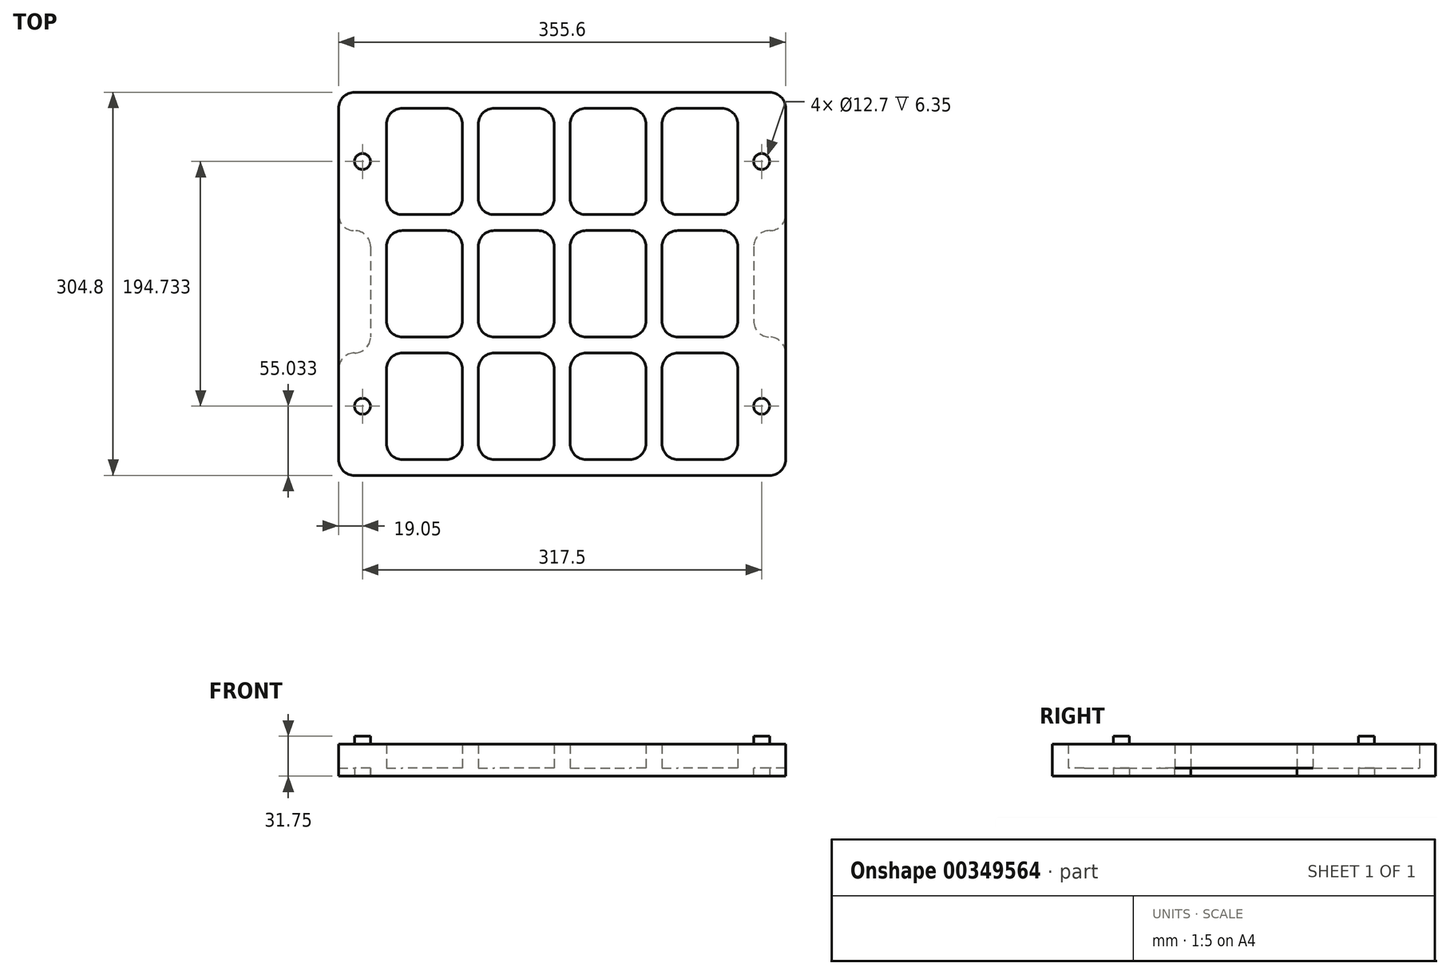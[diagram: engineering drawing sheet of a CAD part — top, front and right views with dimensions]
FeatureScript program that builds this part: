
annotation { "Feature Type Name" : "Feature", "Feature Type Description" : "" }
export const myFeature = defineFeature(function(context is Context, id is Id, definition is map)
    precondition{}
    {
        {
            var Q0;
            Q0=qCreatedBy(makeId("Top.planeOp"),FACE);
            var sketch = newSketch(context, id + "F0", { "sketchPlane" : qUnion([Q0])});
            skLineSegment(sketch, "E0.bottom", {"start": v(165.1, -152.4) * mm, "end": v(-165.1, -152.4) * mm});
            skLineSegment(sketch, "E0.top", {"start": v(165.1, 152.4) * mm, "end": v(-165.1, 152.4) * mm});
            skLineSegment(sketch, "E0.left", {"start": v(177.8, -139.7) * mm, "end": v(177.8, -55.03) * mm});
            skLineSegment(sketch, "E0.right", {"start": v(-177.8, -139.7) * mm, "end": v(-177.8, -67.73) * mm});
            skPoint(sketch, "E0.middle", {"position": v(0, 0) * mm});
            skLineSegment(sketch, "E1", {"start": v(-177.8, 55.03) * mm, "end": v(-177.8, 139.7) * mm});
            skLineSegment(sketch, "E2", {"start": v(177.8, 55.03) * mm, "end": v(177.8, 139.7) * mm});
            skPoint(sketch, "E3.visualSharp", {"position": v(-177.8, 152.4) * mm});
            skArc(sketch, "E3.filletArc", {"start": v(-165.1, 152.4) * mm, "mid": v(-174.08, 148.68) * mm, "end": v(-177.8, 139.7) * mm});
            skPoint(sketch, "E4.visualSharp", {"position": v(-177.8, -152.4) * mm});
            skArc(sketch, "E4.filletArc", {"start": v(-177.8, -139.7) * mm, "mid": v(-174.08, -148.68) * mm, "end": v(-165.1, -152.4) * mm});
            skPoint(sketch, "E5.visualSharp", {"position": v(177.8, -152.4) * mm});
            skArc(sketch, "E5.filletArc", {"start": v(165.1, -152.4) * mm, "mid": v(174.08, -148.68) * mm, "end": v(177.8, -139.7) * mm});
            skPoint(sketch, "E6.visualSharp", {"position": v(177.8, 152.4) * mm});
            skArc(sketch, "E6.filletArc", {"start": v(177.8, 139.7) * mm, "mid": v(174.08, 148.68) * mm, "end": v(165.1, 152.4) * mm});
            skLineSegment(sketch, "E7", {"start": v(-139.7, 139.7) * mm, "end": v(139.7, 139.7) * mm, "construction": true});
            skLineSegment(sketch, "E8", {"start": v(139.7, 139.7) * mm, "end": v(139.7, -139.7) * mm, "construction": true});
            skLineSegment(sketch, "E9", {"start": v(139.7, -139.7) * mm, "end": v(-139.7, -139.7) * mm, "construction": true});
            skLineSegment(sketch, "E10", {"start": v(-139.7, -139.7) * mm, "end": v(-139.7, 139.7) * mm, "construction": true});
            skLineSegment(sketch, "E11", {"start": v(-79.38, 139.7) * mm, "end": v(-79.38, -139.7) * mm, "construction": true});
            skLineSegment(sketch, "E12", {"start": v(-66.68, 139.7) * mm, "end": v(-66.68, -139.7) * mm, "construction": true});
            skLineSegment(sketch, "E13", {"start": v(-6.35, 139.7) * mm, "end": v(-6.35, -139.7) * mm, "construction": true});
            skLineSegment(sketch, "E14", {"start": v(6.35, -139.7) * mm, "end": v(6.35, 139.7) * mm, "construction": true});
            skLineSegment(sketch, "E15", {"start": v(66.67, 139.7) * mm, "end": v(66.67, -139.7) * mm, "construction": true});
            skLineSegment(sketch, "E16", {"start": v(-139.7, 55.03) * mm, "end": v(139.7, 55.03) * mm, "construction": true});
            skLineSegment(sketch, "E17", {"start": v(139.7, 42.33) * mm, "end": v(-139.7, 42.33) * mm, "construction": true});
            skLineSegment(sketch, "E18", {"start": v(-139.7, -42.33) * mm, "end": v(139.7, -42.33) * mm, "construction": true});
            skLineSegment(sketch, "E19", {"start": v(139.7, -55.03) * mm, "end": v(-139.7, -55.03) * mm, "construction": true});
            skLineSegment(sketch, "E20", {"start": v(79.37, 139.7) * mm, "end": v(79.37, -139.7) * mm, "construction": true});
            skLineSegment(sketch, "E21", {"start": v(-139.7, -243.61) * mm, "end": v(-79.38, -243.61) * mm, "construction": true});
            skLineSegment(sketch, "E22", {"start": v(-66.68, -243.61) * mm, "end": v(-6.35, -243.61) * mm, "construction": true});
            skLineSegment(sketch, "E23", {"start": v(6.35, -243.61) * mm, "end": v(66.67, -243.61) * mm, "construction": true});
            skLineSegment(sketch, "E24", {"start": v(79.37, -243.61) * mm, "end": v(139.7, -243.61) * mm, "construction": true});
            skLineSegment(sketch, "E25", {"start": v(300.3, -139.7) * mm, "end": v(300.3, -55.03) * mm, "construction": true});
            skLineSegment(sketch, "E26", {"start": v(300.3, -42.33) * mm, "end": v(300.3, 42.33) * mm, "construction": true});
            skLineSegment(sketch, "E27", {"start": v(300.3, 55.03) * mm, "end": v(300.3, 139.7) * mm, "construction": true});
            skLineSegment(sketch, "E28.bottom", {"start": v(-127, 139.7) * mm, "end": v(-92.08, 139.7) * mm});
            skLineSegment(sketch, "E28.top", {"start": v(-127, 55.03) * mm, "end": v(-92.08, 55.03) * mm});
            skLineSegment(sketch, "E28.left", {"start": v(-139.7, 127) * mm, "end": v(-139.7, 67.73) * mm});
            skLineSegment(sketch, "E28.right", {"start": v(-79.38, 127) * mm, "end": v(-79.38, 67.73) * mm});
            skLineSegment(sketch, "E29.bottom", {"start": v(-92.08, 42.33) * mm, "end": v(-127, 42.33) * mm});
            skLineSegment(sketch, "E29.top", {"start": v(-92.08, -42.33) * mm, "end": v(-127, -42.33) * mm});
            skLineSegment(sketch, "E29.left", {"start": v(-79.38, 29.63) * mm, "end": v(-79.38, -29.63) * mm});
            skLineSegment(sketch, "E29.right", {"start": v(-139.7, 29.63) * mm, "end": v(-139.7, -29.63) * mm});
            skLineSegment(sketch, "E30.bottom", {"start": v(-127, -55.03) * mm, "end": v(-92.08, -55.03) * mm});
            skLineSegment(sketch, "E30.top", {"start": v(-127, -139.7) * mm, "end": v(-92.08, -139.7) * mm});
            skLineSegment(sketch, "E30.left", {"start": v(-139.7, -67.73) * mm, "end": v(-139.7, -127) * mm});
            skLineSegment(sketch, "E30.right", {"start": v(-79.38, -67.73) * mm, "end": v(-79.38, -127) * mm});
            skLineSegment(sketch, "E31.bottom", {"start": v(-53.98, 139.7) * mm, "end": v(-19.05, 139.7) * mm});
            skLineSegment(sketch, "E31.top", {"start": v(-53.98, 55.03) * mm, "end": v(-19.05, 55.03) * mm});
            skLineSegment(sketch, "E31.left", {"start": v(-66.68, 127) * mm, "end": v(-66.68, 67.73) * mm});
            skLineSegment(sketch, "E31.right", {"start": v(-6.35, 127) * mm, "end": v(-6.35, 67.73) * mm});
            skLineSegment(sketch, "E32.bottom", {"start": v(-19.05, 42.33) * mm, "end": v(-53.98, 42.33) * mm});
            skLineSegment(sketch, "E32.top", {"start": v(-19.05, -42.33) * mm, "end": v(-53.98, -42.33) * mm});
            skLineSegment(sketch, "E32.left", {"start": v(-6.35, 29.63) * mm, "end": v(-6.35, -29.63) * mm});
            skLineSegment(sketch, "E32.right", {"start": v(-66.68, 29.63) * mm, "end": v(-66.68, -29.63) * mm});
            skLineSegment(sketch, "E33.bottom", {"start": v(-53.98, -55.03) * mm, "end": v(-19.05, -55.03) * mm});
            skLineSegment(sketch, "E33.top", {"start": v(-53.98, -139.7) * mm, "end": v(-19.05, -139.7) * mm});
            skLineSegment(sketch, "E33.left", {"start": v(-66.68, -67.73) * mm, "end": v(-66.68, -127) * mm});
            skLineSegment(sketch, "E33.right", {"start": v(-6.35, -67.73) * mm, "end": v(-6.35, -127) * mm});
            skLineSegment(sketch, "E34.bottom", {"start": v(19.05, -139.7) * mm, "end": v(53.97, -139.7) * mm});
            skLineSegment(sketch, "E34.top", {"start": v(19.05, -55.03) * mm, "end": v(53.97, -55.03) * mm});
            skLineSegment(sketch, "E34.left", {"start": v(6.35, -127) * mm, "end": v(6.35, -67.73) * mm});
            skLineSegment(sketch, "E34.right", {"start": v(66.67, -127) * mm, "end": v(66.67, -67.73) * mm});
            skPoint(sketch, "E35.oppositeSnap0", {"position": v(0, 42.33) * mm});
            skLineSegment(sketch, "E35.bottom", {"start": v(53.97, -42.33) * mm, "end": v(19.05, -42.33) * mm});
            skLineSegment(sketch, "E35.top", {"start": v(53.97, 42.33) * mm, "end": v(19.05, 42.33) * mm});
            skLineSegment(sketch, "E35.left", {"start": v(66.67, -29.63) * mm, "end": v(66.67, 29.63) * mm});
            skLineSegment(sketch, "E35.right", {"start": v(6.35, -29.63) * mm, "end": v(6.35, 29.63) * mm});
            skLineSegment(sketch, "E36.bottom", {"start": v(19.05, 55.03) * mm, "end": v(53.97, 55.03) * mm});
            skLineSegment(sketch, "E36.top", {"start": v(19.05, 139.7) * mm, "end": v(53.97, 139.7) * mm});
            skLineSegment(sketch, "E36.left", {"start": v(6.35, 67.73) * mm, "end": v(6.35, 127) * mm});
            skLineSegment(sketch, "E36.right", {"start": v(66.67, 67.73) * mm, "end": v(66.67, 127) * mm});
            skLineSegment(sketch, "E37.bottom", {"start": v(92.07, 139.7) * mm, "end": v(127, 139.7) * mm});
            skLineSegment(sketch, "E37.top", {"start": v(92.07, 55.03) * mm, "end": v(127, 55.03) * mm});
            skLineSegment(sketch, "E37.left", {"start": v(79.37, 127) * mm, "end": v(79.37, 67.73) * mm});
            skLineSegment(sketch, "E37.right", {"start": v(139.7, 127) * mm, "end": v(139.7, 67.73) * mm});
            skLineSegment(sketch, "E38.bottom", {"start": v(127, 42.33) * mm, "end": v(92.07, 42.33) * mm});
            skLineSegment(sketch, "E38.top", {"start": v(127, -42.33) * mm, "end": v(92.07, -42.33) * mm});
            skLineSegment(sketch, "E38.left", {"start": v(139.7, 29.63) * mm, "end": v(139.7, -29.63) * mm});
            skLineSegment(sketch, "E38.right", {"start": v(79.37, 29.63) * mm, "end": v(79.37, -29.63) * mm});
            skLineSegment(sketch, "E39.bottom", {"start": v(92.07, -55.03) * mm, "end": v(127, -55.03) * mm});
            skLineSegment(sketch, "E39.top", {"start": v(92.07, -139.7) * mm, "end": v(127, -139.7) * mm});
            skLineSegment(sketch, "E39.left", {"start": v(79.37, -67.73) * mm, "end": v(79.37, -127) * mm});
            skLineSegment(sketch, "E39.right", {"start": v(139.7, -67.73) * mm, "end": v(139.7, -127) * mm});
            skPoint(sketch, "E40.visualSharp", {"position": v(-139.7, 139.7) * mm});
            skArc(sketch, "E40.filletArc", {"start": v(-127, 139.7) * mm, "mid": v(-135.98, 135.98) * mm, "end": v(-139.7, 127) * mm});
            skPoint(sketch, "E41.visualSharp", {"position": v(-79.38, 139.7) * mm});
            skArc(sketch, "E41.filletArc", {"start": v(-79.38, 127) * mm, "mid": v(-83.1, 135.98) * mm, "end": v(-92.08, 139.7) * mm});
            skPoint(sketch, "E42.visualSharp", {"position": v(-66.68, 139.7) * mm});
            skArc(sketch, "E42.filletArc", {"start": v(-53.98, 139.7) * mm, "mid": v(-62.96, 135.98) * mm, "end": v(-66.68, 127) * mm});
            skPoint(sketch, "E43.visualSharp", {"position": v(-6.35, 139.7) * mm});
            skArc(sketch, "E43.filletArc", {"start": v(-6.35, 127) * mm, "mid": v(-10.07, 135.98) * mm, "end": v(-19.05, 139.7) * mm});
            skPoint(sketch, "E44.visualSharp", {"position": v(6.35, 139.7) * mm});
            skArc(sketch, "E44.filletArc", {"start": v(19.05, 139.7) * mm, "mid": v(10.07, 135.98) * mm, "end": v(6.35, 127) * mm});
            skPoint(sketch, "E45.visualSharp", {"position": v(66.67, 139.7) * mm});
            skArc(sketch, "E45.filletArc", {"start": v(66.67, 127) * mm, "mid": v(62.96, 135.98) * mm, "end": v(53.97, 139.7) * mm});
            skPoint(sketch, "E46.visualSharp", {"position": v(79.37, 139.7) * mm});
            skArc(sketch, "E46.filletArc", {"start": v(92.07, 139.7) * mm, "mid": v(83.1, 135.98) * mm, "end": v(79.38, 127) * mm});
            skPoint(sketch, "E47.visualSharp", {"position": v(139.7, 139.7) * mm});
            skArc(sketch, "E47.filletArc", {"start": v(139.7, 127) * mm, "mid": v(135.98, 135.98) * mm, "end": v(127, 139.7) * mm});
            skPoint(sketch, "E48.visualSharp", {"position": v(139.7, 55.03) * mm});
            skArc(sketch, "E48.filletArc", {"start": v(127, 55.03) * mm, "mid": v(135.98, 58.75) * mm, "end": v(139.7, 67.73) * mm});
            skPoint(sketch, "E49.visualSharp", {"position": v(79.37, 55.03) * mm});
            skArc(sketch, "E49.filletArc", {"start": v(79.37, 67.73) * mm, "mid": v(83.1, 58.75) * mm, "end": v(92.07, 55.03) * mm});
            skPoint(sketch, "E50.visualSharp", {"position": v(66.67, 55.03) * mm});
            skArc(sketch, "E50.filletArc", {"start": v(53.97, 55.03) * mm, "mid": v(62.96, 58.75) * mm, "end": v(66.67, 67.73) * mm});
            skPoint(sketch, "E51.visualSharp", {"position": v(-6.35, 55.03) * mm});
            skArc(sketch, "E51.filletArc", {"start": v(-19.05, 55.03) * mm, "mid": v(-10.07, 58.75) * mm, "end": v(-6.35, 67.73) * mm});
            skPoint(sketch, "E52.visualSharp", {"position": v(-66.68, 55.03) * mm});
            skArc(sketch, "E52.filletArc", {"start": v(-66.68, 67.73) * mm, "mid": v(-62.96, 58.75) * mm, "end": v(-53.98, 55.03) * mm});
            skPoint(sketch, "E53.visualSharp", {"position": v(-79.38, 55.03) * mm});
            skArc(sketch, "E53.filletArc", {"start": v(-92.08, 55.03) * mm, "mid": v(-83.1, 58.75) * mm, "end": v(-79.38, 67.73) * mm});
            skPoint(sketch, "E54.visualSharp", {"position": v(-139.7, 55.03) * mm});
            skArc(sketch, "E54.filletArc", {"start": v(-139.7, 67.73) * mm, "mid": v(-135.98, 58.75) * mm, "end": v(-127, 55.03) * mm});
            skPoint(sketch, "E55.visualSharp", {"position": v(-139.7, -42.33) * mm});
            skArc(sketch, "E55.filletArc", {"start": v(-139.7, -29.63) * mm, "mid": v(-135.98, -38.61) * mm, "end": v(-127, -42.33) * mm});
            skPoint(sketch, "E56.visualSharp", {"position": v(-79.38, -42.33) * mm});
            skArc(sketch, "E56.filletArc", {"start": v(-92.08, -42.33) * mm, "mid": v(-83.1, -38.61) * mm, "end": v(-79.38, -29.63) * mm});
            skPoint(sketch, "E57.visualSharp", {"position": v(-66.68, -42.33) * mm});
            skArc(sketch, "E57.filletArc", {"start": v(-66.68, -29.63) * mm, "mid": v(-62.96, -38.61) * mm, "end": v(-53.98, -42.33) * mm});
            skPoint(sketch, "E58.visualSharp", {"position": v(-6.35, -42.33) * mm});
            skArc(sketch, "E58.filletArc", {"start": v(-19.05, -42.33) * mm, "mid": v(-10.07, -38.61) * mm, "end": v(-6.35, -29.63) * mm});
            skPoint(sketch, "E59.visualSharp", {"position": v(6.35, -42.33) * mm});
            skArc(sketch, "E59.filletArc", {"start": v(6.35, -29.63) * mm, "mid": v(10.07, -38.61) * mm, "end": v(19.05, -42.33) * mm});
            skPoint(sketch, "E60.visualSharp", {"position": v(66.67, -42.33) * mm});
            skArc(sketch, "E60.filletArc", {"start": v(53.97, -42.33) * mm, "mid": v(62.96, -38.61) * mm, "end": v(66.67, -29.63) * mm});
            skPoint(sketch, "E61.visualSharp", {"position": v(79.37, -42.33) * mm});
            skArc(sketch, "E61.filletArc", {"start": v(79.37, -29.63) * mm, "mid": v(83.1, -38.61) * mm, "end": v(92.07, -42.33) * mm});
            skPoint(sketch, "E62.visualSharp", {"position": v(139.7, -42.33) * mm});
            skArc(sketch, "E62.filletArc", {"start": v(127, -42.33) * mm, "mid": v(135.98, -38.61) * mm, "end": v(139.7, -29.63) * mm});
            skPoint(sketch, "E63.visualSharp", {"position": v(139.7, -55.03) * mm});
            skArc(sketch, "E63.filletArc", {"start": v(139.7, -67.73) * mm, "mid": v(135.98, -58.75) * mm, "end": v(127, -55.03) * mm});
            skPoint(sketch, "E64.visualSharp", {"position": v(79.37, -55.03) * mm});
            skArc(sketch, "E64.filletArc", {"start": v(92.07, -55.03) * mm, "mid": v(83.1, -58.75) * mm, "end": v(79.37, -67.73) * mm});
            skPoint(sketch, "E65.visualSharp", {"position": v(6.35, -55.03) * mm});
            skArc(sketch, "E65.filletArc", {"start": v(19.05, -55.03) * mm, "mid": v(10.07, -58.75) * mm, "end": v(6.35, -67.73) * mm});
            skPoint(sketch, "E66.visualSharp", {"position": v(-66.68, -55.03) * mm});
            skArc(sketch, "E66.filletArc", {"start": v(-53.98, -55.03) * mm, "mid": v(-62.96, -58.75) * mm, "end": v(-66.68, -67.73) * mm});
            skPoint(sketch, "E67.visualSharp", {"position": v(-6.35, -55.03) * mm});
            skArc(sketch, "E67.filletArc", {"start": v(-6.35, -67.73) * mm, "mid": v(-10.07, -58.75) * mm, "end": v(-19.05, -55.03) * mm});
            skPoint(sketch, "E68.visualSharp", {"position": v(-79.38, -55.03) * mm});
            skArc(sketch, "E68.filletArc", {"start": v(-79.38, -67.73) * mm, "mid": v(-83.1, -58.75) * mm, "end": v(-92.08, -55.03) * mm});
            skPoint(sketch, "E69.visualSharp", {"position": v(-139.7, -55.03) * mm});
            skArc(sketch, "E69.filletArc", {"start": v(-127, -55.03) * mm, "mid": v(-135.98, -58.75) * mm, "end": v(-139.7, -67.73) * mm});
            skPoint(sketch, "E70.visualSharp", {"position": v(-139.7, -139.7) * mm});
            skArc(sketch, "E70.filletArc", {"start": v(-139.7, -127) * mm, "mid": v(-135.98, -135.98) * mm, "end": v(-127, -139.7) * mm});
            skPoint(sketch, "E71.visualSharp", {"position": v(-79.38, -139.7) * mm});
            skArc(sketch, "E71.filletArc", {"start": v(-92.08, -139.7) * mm, "mid": v(-83.1, -135.98) * mm, "end": v(-79.38, -127) * mm});
            skPoint(sketch, "E72.visualSharp", {"position": v(-66.68, -139.7) * mm});
            skArc(sketch, "E72.filletArc", {"start": v(-66.68, -127) * mm, "mid": v(-62.96, -135.98) * mm, "end": v(-53.98, -139.7) * mm});
            skPoint(sketch, "E73.visualSharp", {"position": v(-6.35, -139.7) * mm});
            skArc(sketch, "E73.filletArc", {"start": v(-19.05, -139.7) * mm, "mid": v(-10.07, -135.98) * mm, "end": v(-6.35, -127) * mm});
            skPoint(sketch, "E74.visualSharp", {"position": v(6.35, -139.7) * mm});
            skArc(sketch, "E74.filletArc", {"start": v(6.35, -127) * mm, "mid": v(10.07, -135.98) * mm, "end": v(19.05, -139.7) * mm});
            skPoint(sketch, "E75.visualSharp", {"position": v(66.67, -139.7) * mm});
            skArc(sketch, "E75.filletArc", {"start": v(53.97, -139.7) * mm, "mid": v(62.96, -135.98) * mm, "end": v(66.67, -127) * mm});
            skPoint(sketch, "E76.visualSharp", {"position": v(79.37, -139.7) * mm});
            skArc(sketch, "E76.filletArc", {"start": v(79.37, -127) * mm, "mid": v(83.1, -135.98) * mm, "end": v(92.07, -139.7) * mm});
            skPoint(sketch, "E77.visualSharp", {"position": v(139.7, -139.7) * mm});
            skArc(sketch, "E77.filletArc", {"start": v(127, -139.7) * mm, "mid": v(135.98, -135.98) * mm, "end": v(139.7, -127) * mm});
            skPoint(sketch, "E78.visualSharp", {"position": v(66.67, -55.03) * mm});
            skArc(sketch, "E78.filletArc", {"start": v(66.67, -67.73) * mm, "mid": v(62.96, -58.75) * mm, "end": v(53.97, -55.03) * mm});
            skPoint(sketch, "E79.visualSharp", {"position": v(-139.7, 42.33) * mm});
            skArc(sketch, "E79.filletArc", {"start": v(-127, 42.33) * mm, "mid": v(-135.98, 38.61) * mm, "end": v(-139.7, 29.63) * mm});
            skPoint(sketch, "E80.visualSharp", {"position": v(-79.38, 42.33) * mm});
            skArc(sketch, "E80.filletArc", {"start": v(-79.38, 29.63) * mm, "mid": v(-83.1, 38.61) * mm, "end": v(-92.08, 42.33) * mm});
            skPoint(sketch, "E81.visualSharp", {"position": v(-66.68, 42.33) * mm});
            skArc(sketch, "E81.filletArc", {"start": v(-53.98, 42.33) * mm, "mid": v(-62.96, 38.61) * mm, "end": v(-66.68, 29.63) * mm});
            skPoint(sketch, "E82.visualSharp", {"position": v(-6.35, 42.33) * mm});
            skArc(sketch, "E82.filletArc", {"start": v(-6.35, 29.63) * mm, "mid": v(-10.07, 38.61) * mm, "end": v(-19.05, 42.33) * mm});
            skPoint(sketch, "E83.visualSharp", {"position": v(6.35, 42.33) * mm});
            skArc(sketch, "E83.filletArc", {"start": v(19.05, 42.33) * mm, "mid": v(10.07, 38.61) * mm, "end": v(6.35, 29.63) * mm});
            skPoint(sketch, "E84.visualSharp", {"position": v(66.67, 42.33) * mm});
            skArc(sketch, "E84.filletArc", {"start": v(66.67, 29.63) * mm, "mid": v(62.96, 38.61) * mm, "end": v(53.97, 42.33) * mm});
            skPoint(sketch, "E85.visualSharp", {"position": v(79.37, 42.33) * mm});
            skArc(sketch, "E85.filletArc", {"start": v(92.07, 42.33) * mm, "mid": v(83.1, 38.61) * mm, "end": v(79.37, 29.63) * mm});
            skPoint(sketch, "E86.visualSharp", {"position": v(139.7, 42.33) * mm});
            skArc(sketch, "E86.filletArc", {"start": v(139.7, 29.63) * mm, "mid": v(135.98, 38.61) * mm, "end": v(127, 42.33) * mm});
            skLineSegment(sketch, "E87", {"start": v(-139.7, 97.37) * mm, "end": v(-177.8, 97.37) * mm, "construction": true});
            skLineSegment(sketch, "E88", {"start": v(-139.7, -97.37) * mm, "end": v(-177.8, -97.37) * mm, "construction": true});
            skLineSegment(sketch, "E89", {"start": v(139.7, -97.37) * mm, "end": v(177.8, -97.37) * mm, "construction": true});
            skLineSegment(sketch, "E90", {"start": v(139.7, 97.37) * mm, "end": v(177.8, 97.37) * mm, "construction": true});
            skLineSegment(sketch, "E91.bottom", {"start": v(-177.8, 42.33) * mm, "end": v(-177.8, 42.33) * mm});
            skLineSegment(sketch, "E91.top", {"start": v(-165.1, -55.03) * mm, "end": v(-165.1, -55.03) * mm});
            skLineSegment(sketch, "E91.right", {"start": v(-152.4, 29.63) * mm, "end": v(-152.4, -42.33) * mm});
            skLineSegment(sketch, "E92.bottom", {"start": v(165.1, 42.33) * mm, "end": v(165.1, 42.33) * mm});
            skLineSegment(sketch, "E92.top", {"start": v(165.1, -42.33) * mm, "end": v(165.1, -42.33) * mm});
            skLineSegment(sketch, "E92.right", {"start": v(152.4, 29.63) * mm, "end": v(152.4, -29.63) * mm});
            skPoint(sketch, "E93.visualSharp", {"position": v(-152.4, 42.33) * mm});
            skArc(sketch, "E93.filletArc", {"start": v(-152.4, 29.63) * mm, "mid": v(-156.12, 38.61) * mm, "end": v(-165.1, 42.33) * mm});
            skPoint(sketch, "E94.visualSharp", {"position": v(-152.4, -55.03) * mm});
            skArc(sketch, "E94.filletArc", {"start": v(-165.1, -55.03) * mm, "mid": v(-156.12, -51.31) * mm, "end": v(-152.4, -42.33) * mm});
            skPoint(sketch, "E95.visualSharp", {"position": v(152.4, -42.33) * mm});
            skArc(sketch, "E95.filletArc", {"start": v(152.4, -29.63) * mm, "mid": v(156.12, -38.61) * mm, "end": v(165.1, -42.33) * mm});
            skPoint(sketch, "E96.visualSharp", {"position": v(152.4, 42.33) * mm});
            skArc(sketch, "E96.filletArc", {"start": v(165.1, 42.33) * mm, "mid": v(156.12, 38.61) * mm, "end": v(152.4, 29.63) * mm});
            skPoint(sketch, "E97.visualSharp", {"position": v(6.35, 55.03) * mm});
            skArc(sketch, "E97.filletArc", {"start": v(6.35, 67.73) * mm, "mid": v(10.07, 58.75) * mm, "end": v(19.05, 55.03) * mm});
            skLineSegment(sketch, "E98", {"start": v(-165.1, 42.33) * mm, "end": v(-165.1, 42.33) * mm});
            skPoint(sketch, "E99.visualSharp", {"position": v(-177.8, 42.33) * mm});
            skArc(sketch, "E99.filletArc", {"start": v(-177.8, 55.03) * mm, "mid": v(-174.08, 46.05) * mm, "end": v(-165.1, 42.33) * mm});
            skPoint(sketch, "E100.visualSharp", {"position": v(-177.8, -55.03) * mm});
            skArc(sketch, "E100.filletArc", {"start": v(-165.1, -55.03) * mm, "mid": v(-174.08, -58.75) * mm, "end": v(-177.8, -67.73) * mm});
            skPoint(sketch, "E101.visualSharp", {"position": v(177.8, 42.33) * mm});
            skArc(sketch, "E101.filletArc", {"start": v(165.1, 42.33) * mm, "mid": v(174.08, 46.05) * mm, "end": v(177.8, 55.03) * mm});
            skPoint(sketch, "E102.visualSharp", {"position": v(177.8, -42.33) * mm});
            skArc(sketch, "E102.filletArc", {"start": v(177.8, -55.03) * mm, "mid": v(174.08, -46.05) * mm, "end": v(165.1, -42.33) * mm});
            skLineSegment(sketch, "E103", {"start": v(177.8, 55.03) * mm, "end": v(177.8, -55.03) * mm});
            skLineSegment(sketch, "E104", {"start": v(-177.8, 55.03) * mm, "end": v(-177.8, -67.73) * mm});
            skCircle(sketch, "E105", {"center": v(-158.75, -97.37) * mm, "radius": 6.35 * mm});
            skCircle(sketch, "E106", {"center": v(158.75, 97.37) * mm, "radius": 6.35 * mm});
            skCircle(sketch, "E107", {"center": v(158.75, -97.37) * mm, "radius": 6.35 * mm});
            skCircle(sketch, "E108", {"center": v(-158.75, 97.37) * mm, "radius": 6.35 * mm});
            skSolve(sketch);
        }
        {
            var Q0;
            Q0=makeQuery(id+"F0.imprint","IMPRINT",FACE,{"disambiguationData":[TD([[makeQuery(id+"F0.imprint","IMPRINT",EDGE,{"derivedFrom":sQuery(id+"F0.wireOp",EDGE,"E0.bottom")}),-1.0]])]});
            var Q1;
            Q1=makeQuery(id+"F0.imprint","IMPRINT",FACE,{"disambiguationData":[TD([[makeQuery(id+"F0.imprint","IMPRINT",EDGE,{"derivedFrom":sQuery(id+"F0.wireOp",EDGE,"rO1fTYHY-xebG-N9bd-cNvy-NlipbVquyXpp")}),-1.0]])]});
            var Q2;
            Q2=makeQuery(id+"F0.imprint","IMPRINT",FACE,{"disambiguationData":[TD([[makeQuery(id+"F0.imprint","IMPRINT",EDGE,{"derivedFrom":sQuery(id+"F0.wireOp",EDGE,"pnBWaDpa-4tV1-XdlF-DVXM-y1p302uMCkLa")}),1.0]])]});
            var Q3;
            Q3=makeQuery(id+"F0.imprint","IMPRINT",FACE,{"disambiguationData":[TD([[makeQuery(id+"F0.imprint","IMPRINT",EDGE,{"derivedFrom":sQuery(id+"F0.wireOp",EDGE,"E91.right")}),-1.0]])]});
            var Q4;
            Q4=makeQuery(id+"F0.imprint","IMPRINT",FACE,{"disambiguationData":[TD([[makeQuery(id+"F0.imprint","IMPRINT",EDGE,{"derivedFrom":sQuery(id+"F0.wireOp",EDGE,"E92.right")}),1.0]])]});
            extrude(context, id + "F1", {"entities" : qUnion([Q0, Q1, Q2, Q3, Q4]), "depth" : 19.05 * mm});
        }
        {
            var Q0;
            Q0=makeQuery(id+"F0.imprint","IMPRINT",FACE,{"disambiguationData":[TD([[makeQuery(id+"F0.imprint","IMPRINT",EDGE,{"derivedFrom":sQuery(id+"F0.wireOp",EDGE,"E0.bottom")}),-1.0]])]});
            var Q1;
            Q1=makeQuery(id+"F0.imprint","IMPRINT",FACE,{"disambiguationData":[TD([[makeQuery(id+"F0.imprint","IMPRINT",EDGE,{"derivedFrom":sQuery(id+"F0.wireOp",EDGE,"E28.bottom")}),-1.0]])]});
            var Q2;
            Q2=makeQuery(id+"F0.imprint","IMPRINT",FACE,{"disambiguationData":[TD([[makeQuery(id+"F0.imprint","IMPRINT",EDGE,{"derivedFrom":sQuery(id+"F0.wireOp",EDGE,"E29.bottom")}),1.0]])]});
            var Q3;
            Q3=makeQuery(id+"F0.imprint","IMPRINT",FACE,{"disambiguationData":[TD([[makeQuery(id+"F0.imprint","IMPRINT",EDGE,{"derivedFrom":sQuery(id+"F0.wireOp",EDGE,"E30.bottom")}),-1.0]])]});
            var Q4;
            Q4=makeQuery(id+"F0.imprint","IMPRINT",FACE,{"disambiguationData":[TD([[makeQuery(id+"F0.imprint","IMPRINT",EDGE,{"derivedFrom":sQuery(id+"F0.wireOp",EDGE,"E33.bottom")}),-1.0]])]});
            var Q5;
            Q5=makeQuery(id+"F0.imprint","IMPRINT",FACE,{"disambiguationData":[TD([[makeQuery(id+"F0.imprint","IMPRINT",EDGE,{"derivedFrom":sQuery(id+"F0.wireOp",EDGE,"E31.bottom")}),-1.0]])]});
            var Q6;
            Q6=makeQuery(id+"F0.imprint","IMPRINT",FACE,{"disambiguationData":[TD([[makeQuery(id+"F0.imprint","IMPRINT",EDGE,{"derivedFrom":sQuery(id+"F0.wireOp",EDGE,"E36.bottom")}),1.0]])]});
            var Q7;
            Q7=makeQuery(id+"F0.imprint","IMPRINT",FACE,{"disambiguationData":[TD([[makeQuery(id+"F0.imprint","IMPRINT",EDGE,{"derivedFrom":sQuery(id+"F0.wireOp",EDGE,"E35.bottom")}),-1.0]])]});
            var Q8;
            Q8=makeQuery(id+"F0.imprint","IMPRINT",FACE,{"disambiguationData":[TD([[makeQuery(id+"F0.imprint","IMPRINT",EDGE,{"derivedFrom":sQuery(id+"F0.wireOp",EDGE,"E34.bottom")}),1.0]])]});
            var Q9;
            Q9=makeQuery(id+"F0.imprint","IMPRINT",FACE,{"disambiguationData":[TD([[makeQuery(id+"F0.imprint","IMPRINT",EDGE,{"derivedFrom":sQuery(id+"F0.wireOp",EDGE,"E39.bottom")}),-1.0]])]});
            var Q10;
            Q10=makeQuery(id+"F0.imprint","IMPRINT",FACE,{"disambiguationData":[TD([[makeQuery(id+"F0.imprint","IMPRINT",EDGE,{"derivedFrom":sQuery(id+"F0.wireOp",EDGE,"E38.bottom")}),1.0]])]});
            var Q11;
            Q11=makeQuery(id+"F0.imprint","IMPRINT",FACE,{"disambiguationData":[TD([[makeQuery(id+"F0.imprint","IMPRINT",EDGE,{"derivedFrom":sQuery(id+"F0.wireOp",EDGE,"E37.bottom")}),-1.0]])]});
            var Q12;
            Q12=makeQuery(id+"F0.imprint","IMPRINT",FACE,{"disambiguationData":[TD([[makeQuery(id+"F0.imprint","IMPRINT",EDGE,{"derivedFrom":sQuery(id+"F0.wireOp",EDGE,"E32.bottom")}),1.0]])]});
            extrude(context, id + "F2", {"entities" : qUnion([Q0, Q1, Q2, Q3, Q4, Q5, Q6, Q7, Q8, Q9, Q10, Q11, Q12]), "operationType" : NewBodyOperationType.ADD, "oppositeDirection" : true, "depth" : 6.35 * mm});
        }
        {
            var Q0;
            Q0=makeQuery(id+"F0.imprint","IMPRINT",FACE,{"disambiguationData":[TD([[makeQuery(id+"F0.imprint","IMPRINT",EDGE,{"derivedFrom":sQuery(id+"F0.wireOp",EDGE,"E107")}),1.0]])]});
            var Q1;
            Q1=makeQuery(id+"F0.imprint","IMPRINT",FACE,{"disambiguationData":[TD([[makeQuery(id+"F0.imprint","IMPRINT",EDGE,{"derivedFrom":sQuery(id+"F0.wireOp",EDGE,"E106")}),1.0]])]});
            var Q2;
            Q2=makeQuery(id+"F0.imprint","IMPRINT",FACE,{"disambiguationData":[TD([[makeQuery(id+"F0.imprint","IMPRINT",EDGE,{"derivedFrom":sQuery(id+"F0.wireOp",EDGE,"E105")}),1.0]])]});
            var Q3;
            Q3=makeQuery(id+"F0.imprint","IMPRINT",FACE,{"disambiguationData":[TD([[makeQuery(id+"F0.imprint","IMPRINT",EDGE,{"derivedFrom":sQuery(id+"F0.wireOp",EDGE,"E108")}),1.0]])]});
            extrude(context, id + "F3", {"entities" : qUnion([Q0, Q1, Q2, Q3]), "operationType" : NewBodyOperationType.ADD, "depth" : 25.4 * mm});
        }
    });
